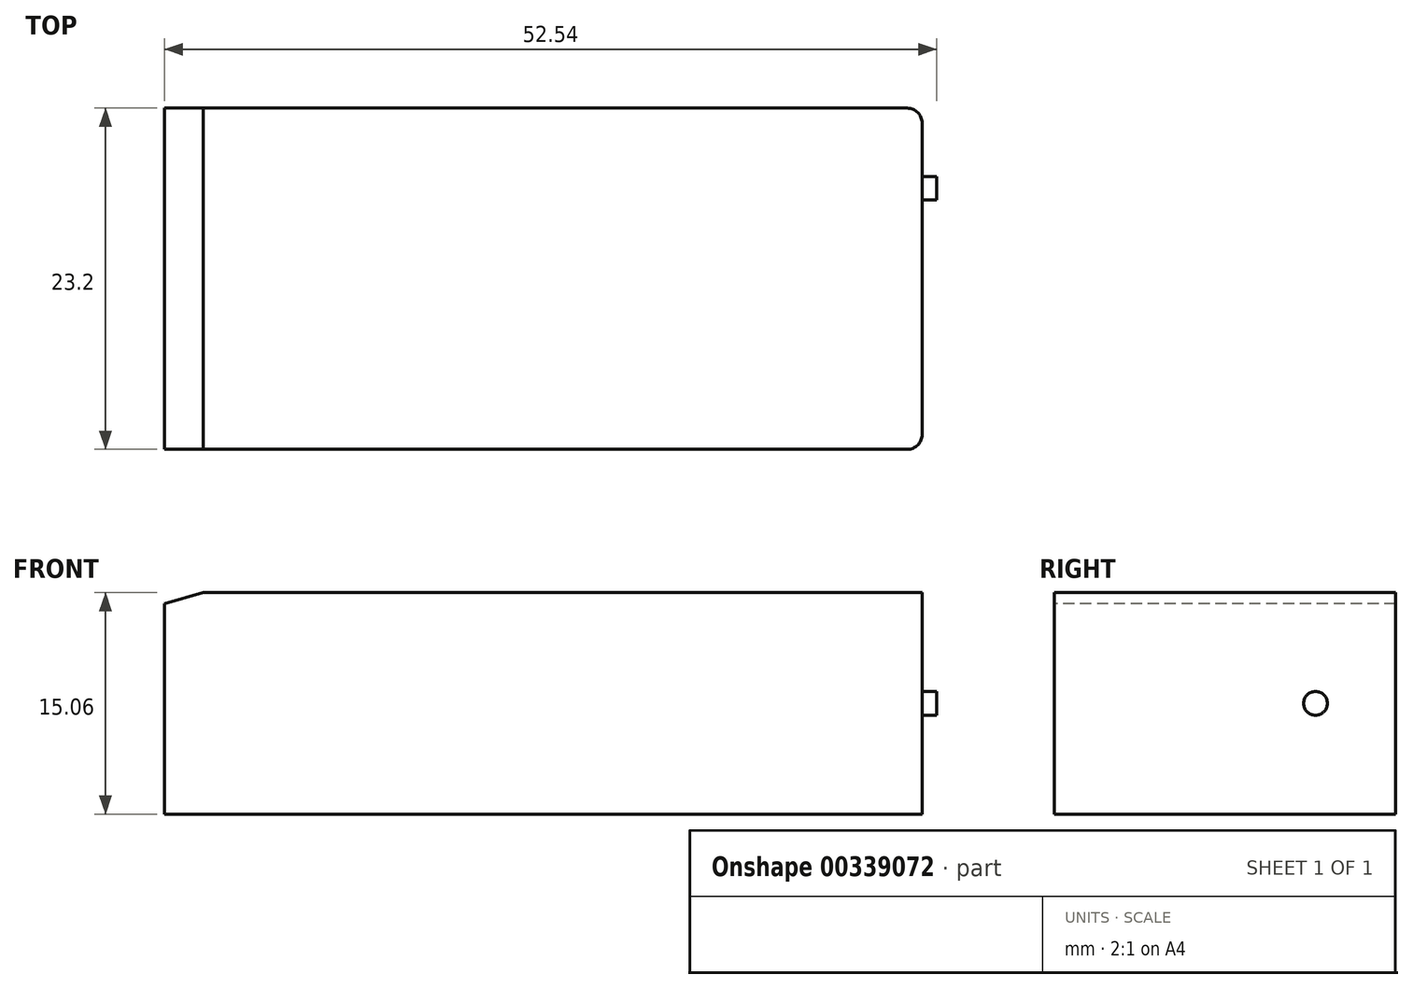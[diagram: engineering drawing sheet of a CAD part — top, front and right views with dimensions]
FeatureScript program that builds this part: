
annotation { "Feature Type Name" : "Feature", "Feature Type Description" : "" }
export const myFeature = defineFeature(function(context is Context, id is Id, definition is map)
    precondition{}
    {
        {
            var Q0;
            Q0=qCreatedBy(makeId("Top.planeOp"),FACE);
            var sketch = newSketch(context, id + "F0", { "sketchPlane" : qUnion([Q0])});
            skLineSegment(sketch, "E0.bottom", {"start": v(25.77, -11.6) * mm, "end": v(-25.77, -11.6) * mm});
            skLineSegment(sketch, "E0.top", {"start": v(25.77, 11.6) * mm, "end": v(-25.77, 11.6) * mm});
            skLineSegment(sketch, "E0.left", {"start": v(25.77, -11.6) * mm, "end": v(25.77, 11.6) * mm});
            skLineSegment(sketch, "E0.right", {"start": v(-25.77, -11.6) * mm, "end": v(-25.77, 11.6) * mm});
            skPoint(sketch, "E0.middle", {"position": v(0, 0) * mm});
            skSolve(sketch);
        }
        {
            var Q0;
            Q0=makeQuery(id+"F0.imprint","IMPRINT",FACE,{"disambiguationData":[TD([[makeQuery(id+"F0.imprint","IMPRINT",EDGE,{"derivedFrom":sQuery(id+"F0.wireOp",EDGE,"E0.bottom")}),-1.0]])]});
            extrude(context, id + "F1", {"entities" : qUnion([Q0]), "depth" : 15.06 * mm, "offsetDistance" : 25 * mm, "symmetric" : true});
        }
        {
            var Q0;
            Q0=makeQuery(id+"F1.opExtrude","SWEPT_EDGE",EDGE,{"disambiguationData":[OSD([sQuery(id+"F0.wireOp",EDGE,"E0.top"),sQuery(id+"F0.wireOp",EDGE,"E0.left")])]});
            var Q1;
            Q1=makeQuery(id+"F1.opExtrude","SWEPT_EDGE",EDGE,{"disambiguationData":[OSD([sQuery(id+"F0.wireOp",EDGE,"E0.bottom"),sQuery(id+"F0.wireOp",EDGE,"E0.left")])]});
            fillet(context, id + "F2", {"entities" : qUnion([Q0, Q1]), "radius" : 1 * mm, "tangentPropagation" : true, "allowEdgeOverflow" : false});
        }
        {
            var Q0;
            Q0=makeQuery(id+"F1.opExtrude","SWEPT_FACE",FACE,{"disambiguationData":[OSD([sQuery(id+"F0.wireOp",EDGE,"E0.left")])]});
            var sketch = newSketch(context, id + "F3", { "sketchPlane" : qUnion([Q0])});
            skCircle(sketch, "E1", {"center": v(6.15, 0) * mm, "radius": 0.8 * mm});
            skSolve(sketch);
        }
        {
            var Q0;
            Q0=makeQuery(id+"F3.imprint","IMPRINT",FACE,{"disambiguationData":[TD([[makeQuery(id+"F3.imprint","IMPRINT",EDGE,{"derivedFrom":sQuery(id+"F3.wireOp",EDGE,"E1")}),1.0]])]});
            extrude(context, id + "F4", {"entities" : qUnion([Q0]), "operationType" : NewBodyOperationType.ADD, "depth" : 1 * mm, "offsetDistance" : 25 * mm});
        }
        {
            var Q0;
            Q0=makeQuery(id+"F1.opExtrude","SWEPT_FACE",FACE,{"disambiguationData":[OSD([sQuery(id+"F0.wireOp",EDGE,"E0.bottom")])]});
            var sketch = newSketch(context, id + "F5", { "sketchPlane" : qUnion([Q0])});
            skLineSegment(sketch, "E2", {"start": v(-25.77, 6.8) * mm, "end": v(-23.1, 7.53) * mm});
            skSolve(sketch);
        }
        {
            var Q0;
            {var subQ0=sQuery(id+"F5.wireOp",EDGE,"E2");Q0=makeQuery(id+"F5.imprint","IMPRINT",FACE,{"disambiguationData":[TD([[makeQuery(id+"F5.imprint","IMPRINT",EDGE,{"derivedFrom":subQ0}),1.0]])]});}
            var Q1;
            Q1=makeQuery(id+"F1.opExtrude","SWEPT_FACE",FACE,{"disambiguationData":[OSD([sQuery(id+"F0.wireOp",EDGE,"E0.top")])]});
            extrude(context, id + "F6", {"entities" : qUnion([Q0]), "operationType" : NewBodyOperationType.REMOVE, "endBound" : BoundingType.UP_TO_SURFACE, "oppositeDirection" : true, "depth" : 25 * mm, "endBoundEntityFace" : qUnion([Q1]), "offsetDistance" : 25 * mm});
        }
    });
